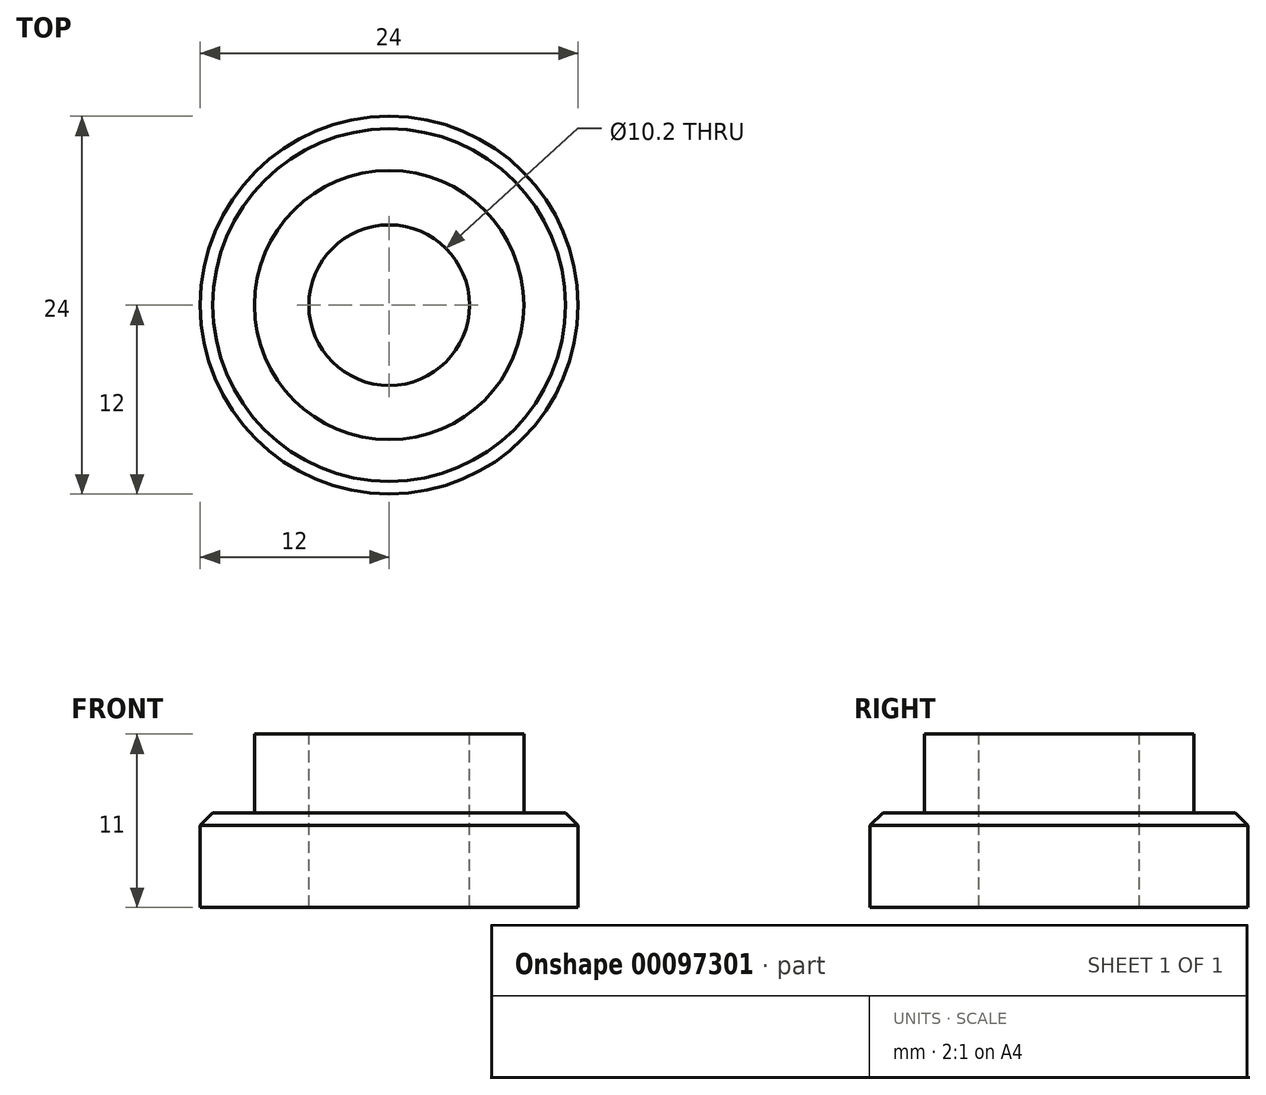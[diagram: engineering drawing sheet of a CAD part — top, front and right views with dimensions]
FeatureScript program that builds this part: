
annotation { "Feature Type Name" : "Feature", "Feature Type Description" : "" }
export const myFeature = defineFeature(function(context is Context, id is Id, definition is map)
    precondition{}
    {
        {
            var Q0;
            Q0=qCreatedBy(makeId("Top.planeOp"),FACE);
            var sketch = newSketch(context, id + "F0", { "sketchPlane" : qUnion([Q0])});
            skCircle(sketch, "E0", {"center": v(0, 0) * mm, "radius": 8.55 * mm});
            skCircle(sketch, "E1", {"center": v(0, 0) * mm, "radius": 12 * mm});
            skSolve(sketch);
        }
        {
            var Q0;
            Q0=makeQuery(id+"F0.imprint","IMPRINT",FACE,{"disambiguationData":[TD([[makeQuery(id+"F0.imprint","IMPRINT",EDGE,{"derivedFrom":sQuery(id+"F0.wireOp",EDGE,"E0")}),1.0]])]});
            extrude(context, id + "F1", {"entities" : qUnion([Q0]), "depth" : 11 * mm});
        }
        {
            var Q0;
            Q0=makeQuery(id+"F0.imprint","IMPRINT",FACE,{"disambiguationData":[TD([[makeQuery(id+"F0.imprint","IMPRINT",EDGE,{"derivedFrom":sQuery(id+"F0.wireOp",EDGE,"E0")}),-1.0]])]});
            extrude(context, id + "F2", {"entities" : qUnion([Q0]), "operationType" : NewBodyOperationType.ADD, "depth" : 6 * mm});
        }
        {
            var Q0;
            Q0=makeQuery(id+"F1.opExtrude","CAP_FACE",FACE,{"disambiguationData":[OSD([sQuery(id+"F0.wireOp",EDGE,"E0")])],"isStart":false});
            var sketch = newSketch(context, id + "F3", { "sketchPlane" : qUnion([Q0])});
            skCircle(sketch, "E2", {"center": v(0, 0) * mm, "radius": 5.1 * mm});
            skSolve(sketch);
        }
        {
            var Q0;
            Q0 = qSketchRegion(id + "F3", true);
            extrude(context, id + "F4", {"entities" : qUnion([Q0]), "operationType" : NewBodyOperationType.REMOVE, "oppositeDirection" : true, "depth" : 25 * mm});
        }
        {
            var Q0;
            Q0=makeQuery(id+"F2.opExtrude","CAP_EDGE",EDGE,{"disambiguationData":[OSD([sQuery(id+"F0.wireOp",EDGE,"E1")])],"isStart":false});
            chamfer(context, id + "F5", {"entities" : qUnion([Q0]), "width" : .8 * mm, "tangentPropagation" : true});
        }
    });
